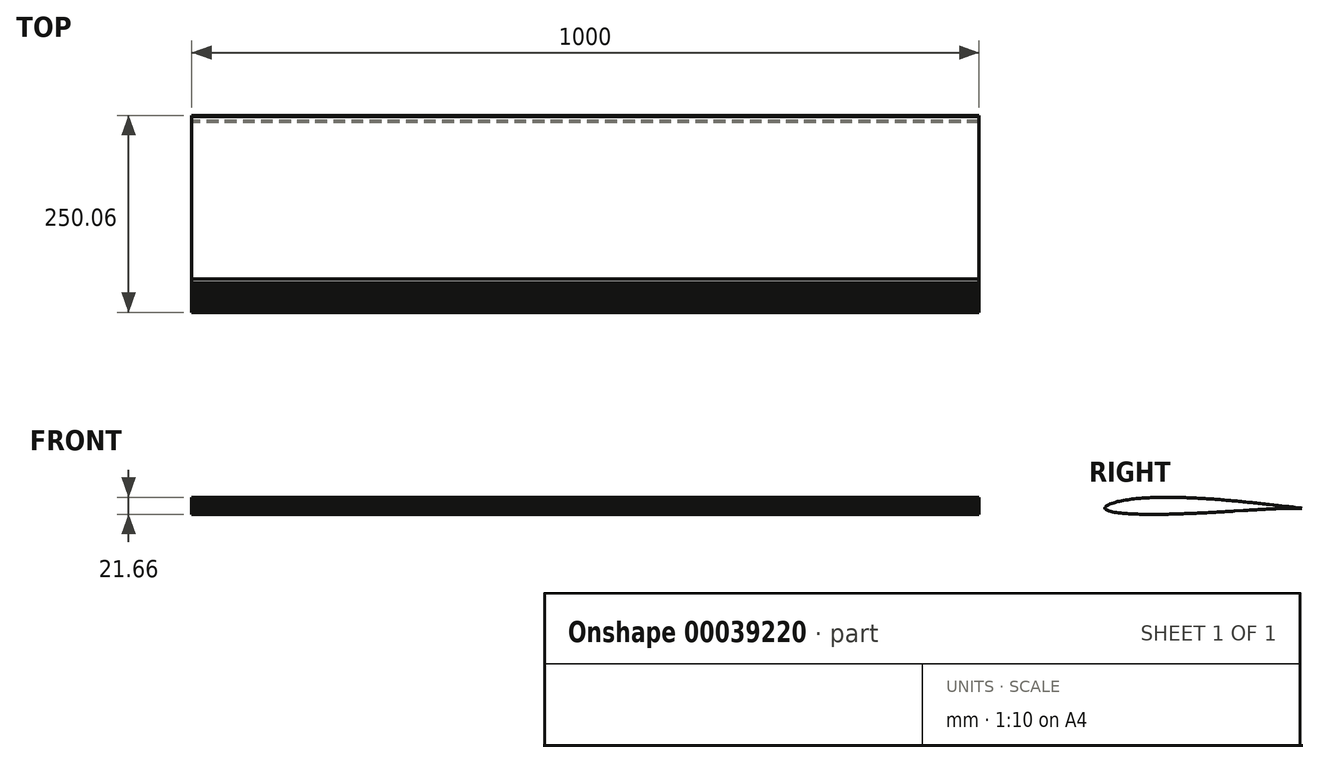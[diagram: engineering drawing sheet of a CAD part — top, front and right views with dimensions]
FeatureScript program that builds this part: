
annotation { "Feature Type Name" : "Feature", "Feature Type Description" : "" }
export const myFeature = defineFeature(function(context is Context, id is Id, definition is map)
    precondition{}
    {
        {
            var Q0;
            Q0=qCreatedBy(makeId("Right.planeOp"),FACE);
            var sketch = newSketch(context, id + "F0", { "sketchPlane" : qUnion([Q0])});
            skLineSegment(sketch, "E0", {"start": v(125.03, -3.1) * mm, "end": v(123.83, -2.95) * mm});
            skLineSegment(sketch, "E1", {"start": v(123.83, -2.95) * mm, "end": v(121.5, -2.66) * mm});
            skLineSegment(sketch, "E2", {"start": v(121.5, -2.66) * mm, "end": v(118.88, -2.32) * mm});
            skLineSegment(sketch, "E3", {"start": v(118.88, -2.32) * mm, "end": v(116.2, -1.99) * mm});
            skLineSegment(sketch, "E4", {"start": v(116.2, -1.99) * mm, "end": v(113.5, -1.67) * mm});
            skLineSegment(sketch, "E5", {"start": v(113.5, -1.67) * mm, "end": v(110.8, -1.35) * mm});
            skLineSegment(sketch, "E6", {"start": v(110.8, -1.35) * mm, "end": v(108.1, -1.03) * mm});
            skLineSegment(sketch, "E7", {"start": v(108.1, -1.03) * mm, "end": v(105.38, -0.72) * mm});
            skLineSegment(sketch, "E8", {"start": v(105.38, -0.72) * mm, "end": v(102.66, -0.4) * mm});
            skLineSegment(sketch, "E9", {"start": v(102.66, -0.4) * mm, "end": v(99.94, -0.1) * mm});
            skLineSegment(sketch, "E10", {"start": v(99.94, -0.1) * mm, "end": v(97.21, 0.2) * mm});
            skLineSegment(sketch, "E11", {"start": v(97.21, 0.2) * mm, "end": v(94.49, 0.52) * mm});
            skLineSegment(sketch, "E12", {"start": v(94.49, 0.52) * mm, "end": v(91.76, 0.82) * mm});
            skLineSegment(sketch, "E13", {"start": v(91.76, 0.82) * mm, "end": v(89.04, 1.12) * mm});
            skLineSegment(sketch, "E14", {"start": v(89.04, 1.12) * mm, "end": v(86.32, 1.42) * mm});
            skLineSegment(sketch, "E15", {"start": v(86.32, 1.42) * mm, "end": v(83.6, 1.72) * mm});
            skLineSegment(sketch, "E16", {"start": v(83.6, 1.72) * mm, "end": v(80.86, 2.02) * mm});
            skLineSegment(sketch, "E17", {"start": v(80.86, 2.02) * mm, "end": v(78.14, 2.32) * mm});
            skLineSegment(sketch, "E18", {"start": v(78.14, 2.32) * mm, "end": v(75.41, 2.61) * mm});
            skLineSegment(sketch, "E19", {"start": v(75.41, 2.61) * mm, "end": v(72.7, 2.9) * mm});
            skLineSegment(sketch, "E20", {"start": v(72.7, 2.9) * mm, "end": v(69.96, 3.2) * mm});
            skLineSegment(sketch, "E21", {"start": v(69.96, 3.2) * mm, "end": v(67.24, 3.48) * mm});
            skLineSegment(sketch, "E22", {"start": v(67.24, 3.48) * mm, "end": v(64.5, 3.77) * mm});
            skLineSegment(sketch, "E23", {"start": v(64.5, 3.77) * mm, "end": v(61.78, 4.05) * mm});
            skLineSegment(sketch, "E24", {"start": v(61.78, 4.05) * mm, "end": v(59.05, 4.33) * mm});
            skLineSegment(sketch, "E25", {"start": v(59.05, 4.33) * mm, "end": v(56.33, 4.6) * mm});
            skLineSegment(sketch, "E26", {"start": v(56.33, 4.6) * mm, "end": v(53.6, 4.88) * mm});
            skLineSegment(sketch, "E27", {"start": v(53.6, 4.88) * mm, "end": v(50.87, 5.15) * mm});
            skLineSegment(sketch, "E28", {"start": v(50.87, 5.15) * mm, "end": v(48.14, 5.42) * mm});
            skLineSegment(sketch, "E29", {"start": v(48.14, 5.42) * mm, "end": v(45.4, 5.68) * mm});
            skLineSegment(sketch, "E30", {"start": v(45.4, 5.68) * mm, "end": v(42.68, 5.95) * mm});
            skLineSegment(sketch, "E31", {"start": v(42.68, 5.95) * mm, "end": v(39.95, 6.2) * mm});
            skLineSegment(sketch, "E32", {"start": v(39.95, 6.2) * mm, "end": v(37.22, 6.46) * mm});
            skLineSegment(sketch, "E33", {"start": v(37.22, 6.46) * mm, "end": v(34.5, 6.7) * mm});
            skLineSegment(sketch, "E34", {"start": v(34.5, 6.7) * mm, "end": v(31.76, 6.95) * mm});
            skLineSegment(sketch, "E35", {"start": v(31.76, 6.95) * mm, "end": v(29.03, 7.2) * mm});
            skLineSegment(sketch, "E36", {"start": v(29.03, 7.2) * mm, "end": v(26.3, 7.43) * mm});
            skLineSegment(sketch, "E37", {"start": v(26.3, 7.43) * mm, "end": v(23.57, 7.66) * mm});
            skLineSegment(sketch, "E38", {"start": v(23.57, 7.66) * mm, "end": v(20.84, 7.87) * mm});
            skLineSegment(sketch, "E39", {"start": v(20.84, 7.87) * mm, "end": v(18.1, 8.09) * mm});
            skLineSegment(sketch, "E40", {"start": v(18.1, 8.09) * mm, "end": v(15.38, 8.3) * mm});
            skLineSegment(sketch, "E41", {"start": v(15.38, 8.3) * mm, "end": v(12.65, 8.5) * mm});
            skLineSegment(sketch, "E42", {"start": v(12.65, 8.5) * mm, "end": v(9.91, 8.69) * mm});
            skLineSegment(sketch, "E43", {"start": v(9.91, 8.69) * mm, "end": v(7.18, 8.87) * mm});
            skLineSegment(sketch, "E44", {"start": v(7.18, 8.87) * mm, "end": v(4.45, 9.04) * mm});
            skLineSegment(sketch, "E45", {"start": v(4.45, 9.04) * mm, "end": v(1.72, 9.22) * mm});
            skLineSegment(sketch, "E46", {"start": v(1.72, 9.22) * mm, "end": v(-1, 9.38) * mm});
            skLineSegment(sketch, "E47", {"start": v(-1, 9.38) * mm, "end": v(-3.74, 9.53) * mm});
            skLineSegment(sketch, "E48", {"start": v(-3.74, 9.53) * mm, "end": v(-6.47, 9.68) * mm});
            skLineSegment(sketch, "E49", {"start": v(-6.47, 9.68) * mm, "end": v(-9.2, 9.82) * mm});
            skLineSegment(sketch, "E50", {"start": v(-9.2, 9.82) * mm, "end": v(-11.93, 9.96) * mm});
            skLineSegment(sketch, "E51", {"start": v(-11.93, 9.96) * mm, "end": v(-14.66, 10.08) * mm});
            skLineSegment(sketch, "E52", {"start": v(-14.66, 10.08) * mm, "end": v(-17.4, 10.2) * mm});
            skLineSegment(sketch, "E53", {"start": v(-17.4, 10.2) * mm, "end": v(-20.12, 10.3) * mm});
            skLineSegment(sketch, "E54", {"start": v(-20.12, 10.3) * mm, "end": v(-22.85, 10.4) * mm});
            skLineSegment(sketch, "E55", {"start": v(-22.85, 10.4) * mm, "end": v(-25.58, 10.5) * mm});
            skLineSegment(sketch, "E56", {"start": v(-25.58, 10.5) * mm, "end": v(-28.31, 10.58) * mm});
            skLineSegment(sketch, "E57", {"start": v(-28.31, 10.58) * mm, "end": v(-31.04, 10.65) * mm});
            skLineSegment(sketch, "E58", {"start": v(-31.04, 10.65) * mm, "end": v(-33.77, 10.7) * mm});
            skLineSegment(sketch, "E59", {"start": v(-33.77, 10.7) * mm, "end": v(-36.5, 10.76) * mm});
            skLineSegment(sketch, "E60", {"start": v(-36.5, 10.76) * mm, "end": v(-39.22, 10.8) * mm});
            skLineSegment(sketch, "E61", {"start": v(-39.22, 10.8) * mm, "end": v(-41.95, 10.82) * mm});
            skLineSegment(sketch, "E62", {"start": v(-41.95, 10.82) * mm, "end": v(-44.67, 10.83) * mm});
            skLineSegment(sketch, "E63", {"start": v(-44.67, 10.83) * mm, "end": v(-47.4, 10.83) * mm});
            skLineSegment(sketch, "E64", {"start": v(-47.4, 10.83) * mm, "end": v(-50.12, 10.82) * mm});
            skLineSegment(sketch, "E65", {"start": v(-50.12, 10.82) * mm, "end": v(-52.84, 10.8) * mm});
            skLineSegment(sketch, "E66", {"start": v(-52.84, 10.8) * mm, "end": v(-55.56, 10.76) * mm});
            skLineSegment(sketch, "E67", {"start": v(-55.56, 10.76) * mm, "end": v(-58.28, 10.7) * mm});
            skLineSegment(sketch, "E68", {"start": v(-58.28, 10.7) * mm, "end": v(-61, 10.63) * mm});
            skLineSegment(sketch, "E69", {"start": v(-61, 10.63) * mm, "end": v(-63.7, 10.54) * mm});
            skLineSegment(sketch, "E70", {"start": v(-63.7, 10.54) * mm, "end": v(-66.42, 10.44) * mm});
            skLineSegment(sketch, "E71", {"start": v(-66.42, 10.44) * mm, "end": v(-69.13, 10.32) * mm});
            skLineSegment(sketch, "E72", {"start": v(-69.13, 10.32) * mm, "end": v(-71.84, 10.17) * mm});
            skLineSegment(sketch, "E73", {"start": v(-71.84, 10.17) * mm, "end": v(-74.53, 10.01) * mm});
            skLineSegment(sketch, "E74", {"start": v(-74.53, 10.01) * mm, "end": v(-77.24, 9.83) * mm});
            skLineSegment(sketch, "E75", {"start": v(-77.24, 9.83) * mm, "end": v(-79.93, 9.62) * mm});
            skLineSegment(sketch, "E76", {"start": v(-79.93, 9.62) * mm, "end": v(-82.62, 9.4) * mm});
            skLineSegment(sketch, "E77", {"start": v(-82.62, 9.4) * mm, "end": v(-85.3, 9.14) * mm});
            skLineSegment(sketch, "E78", {"start": v(-85.3, 9.14) * mm, "end": v(-87.98, 8.86) * mm});
            skLineSegment(sketch, "E79", {"start": v(-87.98, 8.86) * mm, "end": v(-90.65, 8.55) * mm});
            skLineSegment(sketch, "E80", {"start": v(-90.65, 8.55) * mm, "end": v(-93.3, 8.21) * mm});
            skLineSegment(sketch, "E81", {"start": v(-93.3, 8.21) * mm, "end": v(-95.95, 7.83) * mm});
            skLineSegment(sketch, "E82", {"start": v(-95.95, 7.83) * mm, "end": v(-98.59, 7.42) * mm});
            skLineSegment(sketch, "E83", {"start": v(-98.59, 7.42) * mm, "end": v(-101.2, 6.97) * mm});
            skLineSegment(sketch, "E84", {"start": v(-101.2, 6.97) * mm, "end": v(-103.8, 6.47) * mm});
            skLineSegment(sketch, "E85", {"start": v(-103.8, 6.47) * mm, "end": v(-106.37, 5.92) * mm});
            skLineSegment(sketch, "E86", {"start": v(-106.37, 5.92) * mm, "end": v(-108.92, 5.31) * mm});
            skLineSegment(sketch, "E87", {"start": v(-108.92, 5.31) * mm, "end": v(-111.41, 4.64) * mm});
            skLineSegment(sketch, "E88", {"start": v(-111.41, 4.64) * mm, "end": v(-113.85, 3.9) * mm});
            skLineSegment(sketch, "E89", {"start": v(-113.85, 3.9) * mm, "end": v(-116.19, 3.1) * mm});
            skLineSegment(sketch, "E90", {"start": v(-116.19, 3.1) * mm, "end": v(-118.4, 2.23) * mm});
            skLineSegment(sketch, "E91", {"start": v(-118.4, 2.23) * mm, "end": v(-120.37, 1.3) * mm});
            skLineSegment(sketch, "E92", {"start": v(-120.37, 1.3) * mm, "end": v(-121.94, 0.4) * mm});
            skLineSegment(sketch, "E93", {"start": v(-121.94, 0.4) * mm, "end": v(-123.05, -0.37) * mm});
            skLineSegment(sketch, "E94", {"start": v(-123.05, -0.37) * mm, "end": v(-123.8, -0.98) * mm});
            skLineSegment(sketch, "E95", {"start": v(-123.8, -0.98) * mm, "end": v(-124.3, -1.47) * mm});
            skLineSegment(sketch, "E96", {"start": v(-124.3, -1.47) * mm, "end": v(-124.63, -1.88) * mm});
            skLineSegment(sketch, "E97", {"start": v(-124.63, -1.88) * mm, "end": v(-124.86, -2.28) * mm});
            skLineSegment(sketch, "E98", {"start": v(-124.86, -2.28) * mm, "end": v(-125, -2.78) * mm});
            skLineSegment(sketch, "E99", {"start": v(-125, -2.78) * mm, "end": v(-125.03, -3.1) * mm});
            skLineSegment(sketch, "E100", {"start": v(-125.03, -3.1) * mm, "end": v(-125.03, -3.13) * mm});
            skLineSegment(sketch, "E101", {"start": v(-125.03, -3.13) * mm, "end": v(-124.97, -3.3) * mm});
            skLineSegment(sketch, "E102", {"start": v(-124.97, -3.3) * mm, "end": v(-124.8, -3.64) * mm});
            skLineSegment(sketch, "E103", {"start": v(-124.8, -3.64) * mm, "end": v(-124.53, -4.02) * mm});
            skLineSegment(sketch, "E104", {"start": v(-124.53, -4.02) * mm, "end": v(-124.13, -4.38) * mm});
            skLineSegment(sketch, "E105", {"start": v(-124.13, -4.38) * mm, "end": v(-123.55, -4.78) * mm});
            skLineSegment(sketch, "E106", {"start": v(-123.55, -4.78) * mm, "end": v(-122.71, -5.24) * mm});
            skLineSegment(sketch, "E107", {"start": v(-122.71, -5.24) * mm, "end": v(-121.47, -5.8) * mm});
            skLineSegment(sketch, "E108", {"start": v(-121.47, -5.8) * mm, "end": v(-119.72, -6.44) * mm});
            skLineSegment(sketch, "E109", {"start": v(-119.72, -6.44) * mm, "end": v(-117.58, -7.06) * mm});
            skLineSegment(sketch, "E110", {"start": v(-117.58, -7.06) * mm, "end": v(-115.22, -7.6) * mm});
            skLineSegment(sketch, "E111", {"start": v(-115.22, -7.6) * mm, "end": v(-112.73, -8.08) * mm});
            skLineSegment(sketch, "E112", {"start": v(-112.73, -8.08) * mm, "end": v(-110.17, -8.5) * mm});
            skLineSegment(sketch, "E113", {"start": v(-110.17, -8.5) * mm, "end": v(-107.58, -8.86) * mm});
            skLineSegment(sketch, "E114", {"start": v(-107.58, -8.86) * mm, "end": v(-104.95, -9.17) * mm});
            skLineSegment(sketch, "E115", {"start": v(-104.95, -9.17) * mm, "end": v(-102.3, -9.44) * mm});
            skLineSegment(sketch, "E116", {"start": v(-102.3, -9.44) * mm, "end": v(-99.63, -9.68) * mm});
            skLineSegment(sketch, "E117", {"start": v(-99.63, -9.68) * mm, "end": v(-96.95, -9.88) * mm});
            skLineSegment(sketch, "E118", {"start": v(-96.95, -9.88) * mm, "end": v(-94.26, -10.06) * mm});
            skLineSegment(sketch, "E119", {"start": v(-94.26, -10.06) * mm, "end": v(-91.56, -10.22) * mm});
            skLineSegment(sketch, "E120", {"start": v(-91.56, -10.22) * mm, "end": v(-88.85, -10.35) * mm});
            skLineSegment(sketch, "E121", {"start": v(-88.85, -10.35) * mm, "end": v(-86.14, -10.46) * mm});
            skLineSegment(sketch, "E122", {"start": v(-86.14, -10.46) * mm, "end": v(-83.43, -10.56) * mm});
            skLineSegment(sketch, "E123", {"start": v(-83.43, -10.56) * mm, "end": v(-80.71, -10.64) * mm});
            skLineSegment(sketch, "E124", {"start": v(-80.71, -10.64) * mm, "end": v(-78, -10.7) * mm});
            skLineSegment(sketch, "E125", {"start": v(-78, -10.7) * mm, "end": v(-75.27, -10.75) * mm});
            skLineSegment(sketch, "E126", {"start": v(-75.27, -10.75) * mm, "end": v(-72.54, -10.8) * mm});
            skLineSegment(sketch, "E127", {"start": v(-72.54, -10.8) * mm, "end": v(-69.81, -10.82) * mm});
            skLineSegment(sketch, "E128", {"start": v(-69.81, -10.82) * mm, "end": v(-67.09, -10.83) * mm});
            skLineSegment(sketch, "E129", {"start": v(-67.09, -10.83) * mm, "end": v(-64.36, -10.83) * mm});
            skLineSegment(sketch, "E130", {"start": v(-64.36, -10.83) * mm, "end": v(-61.62, -10.83) * mm});
            skLineSegment(sketch, "E131", {"start": v(-61.62, -10.83) * mm, "end": v(-58.89, -10.81) * mm});
            skLineSegment(sketch, "E132", {"start": v(-58.89, -10.81) * mm, "end": v(-56.15, -10.79) * mm});
            skLineSegment(sketch, "E133", {"start": v(-56.15, -10.79) * mm, "end": v(-53.42, -10.75) * mm});
            skLineSegment(sketch, "E134", {"start": v(-53.42, -10.75) * mm, "end": v(-50.68, -10.71) * mm});
            skLineSegment(sketch, "E135", {"start": v(-50.68, -10.71) * mm, "end": v(-47.95, -10.66) * mm});
            skLineSegment(sketch, "E136", {"start": v(-47.95, -10.66) * mm, "end": v(-45.21, -10.6) * mm});
            skLineSegment(sketch, "E137", {"start": v(-45.21, -10.6) * mm, "end": v(-42.47, -10.54) * mm});
            skLineSegment(sketch, "E138", {"start": v(-42.47, -10.54) * mm, "end": v(-39.73, -10.47) * mm});
            skLineSegment(sketch, "E139", {"start": v(-39.73, -10.47) * mm, "end": v(-37, -10.4) * mm});
            skLineSegment(sketch, "E140", {"start": v(-37, -10.4) * mm, "end": v(-34.25, -10.31) * mm});
            skLineSegment(sketch, "E141", {"start": v(-34.25, -10.31) * mm, "end": v(-31.52, -10.23) * mm});
            skLineSegment(sketch, "E142", {"start": v(-31.52, -10.23) * mm, "end": v(-28.77, -10.13) * mm});
            skLineSegment(sketch, "E143", {"start": v(-28.77, -10.13) * mm, "end": v(-26.03, -10.03) * mm});
            skLineSegment(sketch, "E144", {"start": v(-26.03, -10.03) * mm, "end": v(-23.3, -9.93) * mm});
            skLineSegment(sketch, "E145", {"start": v(-23.3, -9.93) * mm, "end": v(-20.55, -9.82) * mm});
            skLineSegment(sketch, "E146", {"start": v(-20.55, -9.82) * mm, "end": v(-17.81, -9.7) * mm});
            skLineSegment(sketch, "E147", {"start": v(-17.81, -9.7) * mm, "end": v(-15.07, -9.6) * mm});
            skLineSegment(sketch, "E148", {"start": v(-15.07, -9.6) * mm, "end": v(-12.33, -9.47) * mm});
            skLineSegment(sketch, "E149", {"start": v(-12.33, -9.47) * mm, "end": v(-9.6, -9.35) * mm});
            skLineSegment(sketch, "E150", {"start": v(-9.6, -9.35) * mm, "end": v(-6.85, -9.23) * mm});
            skLineSegment(sketch, "E151", {"start": v(-6.85, -9.23) * mm, "end": v(-4.11, -9.1) * mm});
            skLineSegment(sketch, "E152", {"start": v(-4.11, -9.1) * mm, "end": v(-1.37, -8.96) * mm});
            skLineSegment(sketch, "E153", {"start": v(-1.37, -8.96) * mm, "end": v(1.37, -8.83) * mm});
            skLineSegment(sketch, "E154", {"start": v(1.37, -8.83) * mm, "end": v(4.11, -8.7) * mm});
            skLineSegment(sketch, "E155", {"start": v(4.11, -8.7) * mm, "end": v(6.85, -8.55) * mm});
            skLineSegment(sketch, "E156", {"start": v(6.85, -8.55) * mm, "end": v(9.59, -8.4) * mm});
            skLineSegment(sketch, "E157", {"start": v(9.59, -8.4) * mm, "end": v(12.32, -8.26) * mm});
            skLineSegment(sketch, "E158", {"start": v(12.32, -8.26) * mm, "end": v(15.06, -8.11) * mm});
            skLineSegment(sketch, "E159", {"start": v(15.06, -8.11) * mm, "end": v(17.8, -7.96) * mm});
            skLineSegment(sketch, "E160", {"start": v(17.8, -7.96) * mm, "end": v(20.53, -7.8) * mm});
            skLineSegment(sketch, "E161", {"start": v(20.53, -7.8) * mm, "end": v(23.27, -7.64) * mm});
            skLineSegment(sketch, "E162", {"start": v(23.27, -7.64) * mm, "end": v(26, -7.48) * mm});
            skLineSegment(sketch, "E163", {"start": v(26, -7.48) * mm, "end": v(28.75, -7.3) * mm});
            skLineSegment(sketch, "E164", {"start": v(28.75, -7.3) * mm, "end": v(31.49, -7.14) * mm});
            skLineSegment(sketch, "E165", {"start": v(31.49, -7.14) * mm, "end": v(34.23, -6.96) * mm});
            skLineSegment(sketch, "E166", {"start": v(34.23, -6.96) * mm, "end": v(36.97, -6.8) * mm});
            skLineSegment(sketch, "E167", {"start": v(36.97, -6.8) * mm, "end": v(39.72, -6.62) * mm});
            skLineSegment(sketch, "E168", {"start": v(39.72, -6.62) * mm, "end": v(42.46, -6.44) * mm});
            skLineSegment(sketch, "E169", {"start": v(42.46, -6.44) * mm, "end": v(45.2, -6.27) * mm});
            skLineSegment(sketch, "E170", {"start": v(45.2, -6.27) * mm, "end": v(47.95, -6.1) * mm});
            skLineSegment(sketch, "E171", {"start": v(47.95, -6.1) * mm, "end": v(50.7, -5.92) * mm});
            skLineSegment(sketch, "E172", {"start": v(50.7, -5.92) * mm, "end": v(53.44, -5.75) * mm});
            skLineSegment(sketch, "E173", {"start": v(53.44, -5.75) * mm, "end": v(56.19, -5.58) * mm});
            skLineSegment(sketch, "E174", {"start": v(56.19, -5.58) * mm, "end": v(58.93, -5.42) * mm});
            skLineSegment(sketch, "E175", {"start": v(58.93, -5.42) * mm, "end": v(61.68, -5.25) * mm});
            skLineSegment(sketch, "E176", {"start": v(61.68, -5.25) * mm, "end": v(64.42, -5.1) * mm});
            skLineSegment(sketch, "E177", {"start": v(64.42, -5.1) * mm, "end": v(67.16, -4.93) * mm});
            skLineSegment(sketch, "E178", {"start": v(67.16, -4.93) * mm, "end": v(69.9, -4.78) * mm});
            skLineSegment(sketch, "E179", {"start": v(69.9, -4.78) * mm, "end": v(72.64, -4.63) * mm});
            skLineSegment(sketch, "E180", {"start": v(72.64, -4.63) * mm, "end": v(75.38, -4.48) * mm});
            skLineSegment(sketch, "E181", {"start": v(75.38, -4.48) * mm, "end": v(78.12, -4.34) * mm});
            skLineSegment(sketch, "E182", {"start": v(78.12, -4.34) * mm, "end": v(80.86, -4.2) * mm});
            skLineSegment(sketch, "E183", {"start": v(80.86, -4.2) * mm, "end": v(83.6, -4.06) * mm});
            skLineSegment(sketch, "E184", {"start": v(83.6, -4.06) * mm, "end": v(86.34, -3.93) * mm});
            skLineSegment(sketch, "E185", {"start": v(86.34, -3.93) * mm, "end": v(89.07, -3.8) * mm});
            skLineSegment(sketch, "E186", {"start": v(89.07, -3.8) * mm, "end": v(91.81, -3.7) * mm});
            skLineSegment(sketch, "E187", {"start": v(91.81, -3.7) * mm, "end": v(94.54, -3.58) * mm});
            skLineSegment(sketch, "E188", {"start": v(94.54, -3.58) * mm, "end": v(97.28, -3.48) * mm});
            skLineSegment(sketch, "E189", {"start": v(97.28, -3.48) * mm, "end": v(100, -3.38) * mm});
            skLineSegment(sketch, "E190", {"start": v(100, -3.38) * mm, "end": v(102.74, -3.3) * mm});
            skLineSegment(sketch, "E191", {"start": v(102.74, -3.3) * mm, "end": v(105.47, -3.22) * mm});
            skLineSegment(sketch, "E192", {"start": v(105.47, -3.22) * mm, "end": v(108.2, -3.16) * mm});
            skLineSegment(sketch, "E193", {"start": v(108.2, -3.16) * mm, "end": v(110.91, -3.1) * mm});
            skLineSegment(sketch, "E194", {"start": v(110.91, -3.1) * mm, "end": v(113.63, -3.06) * mm});
            skLineSegment(sketch, "E195", {"start": v(113.63, -3.06) * mm, "end": v(116.3, -3.02) * mm});
            skLineSegment(sketch, "E196", {"start": v(116.3, -3.02) * mm, "end": v(118.92, -3.02) * mm});
            skLineSegment(sketch, "E197", {"start": v(118.92, -3.02) * mm, "end": v(121.49, -3.05) * mm});
            skLineSegment(sketch, "E198", {"start": v(121.49, -3.05) * mm, "end": v(123.82, -3.1) * mm});
            skLineSegment(sketch, "E199", {"start": v(123.82, -3.1) * mm, "end": v(125.03, -3.13) * mm});
            skLineSegment(sketch, "E200", {"start": v(125.03, -3.13) * mm, "end": v(125.03, -3.1) * mm});
            skLineSegment(sketch, "E201", {"start": v(125.03, -3.1) * mm, "end": v(-124.97, -3.3) * mm});
            skSolve(sketch);
        }
        {
            var Q0;
            {var subQ6=sQuery(id+"F0.wireOp",EDGE,"E0");Q0=makeQuery(id+"F0.imprint","IMPRINT",FACE,{"disambiguationData":[TD([[makeQuery(id+"F0.imprint","IMPRINT",EDGE,{"derivedFrom":subQ6}),1.0]])]});}
            var Q1;
            {var subQ4=sQuery(id+"F0.wireOp",EDGE,"E102");Q1=makeQuery(id+"F0.imprint","IMPRINT",FACE,{"disambiguationData":[TD([[makeQuery(id+"F0.imprint","IMPRINT",EDGE,{"derivedFrom":subQ4}),1.0]])]});}
            extrude(context, id + "F1", {"entities" : qUnion([Q0, Q1]), "depth" : 1000 * mm});
        }
    });
